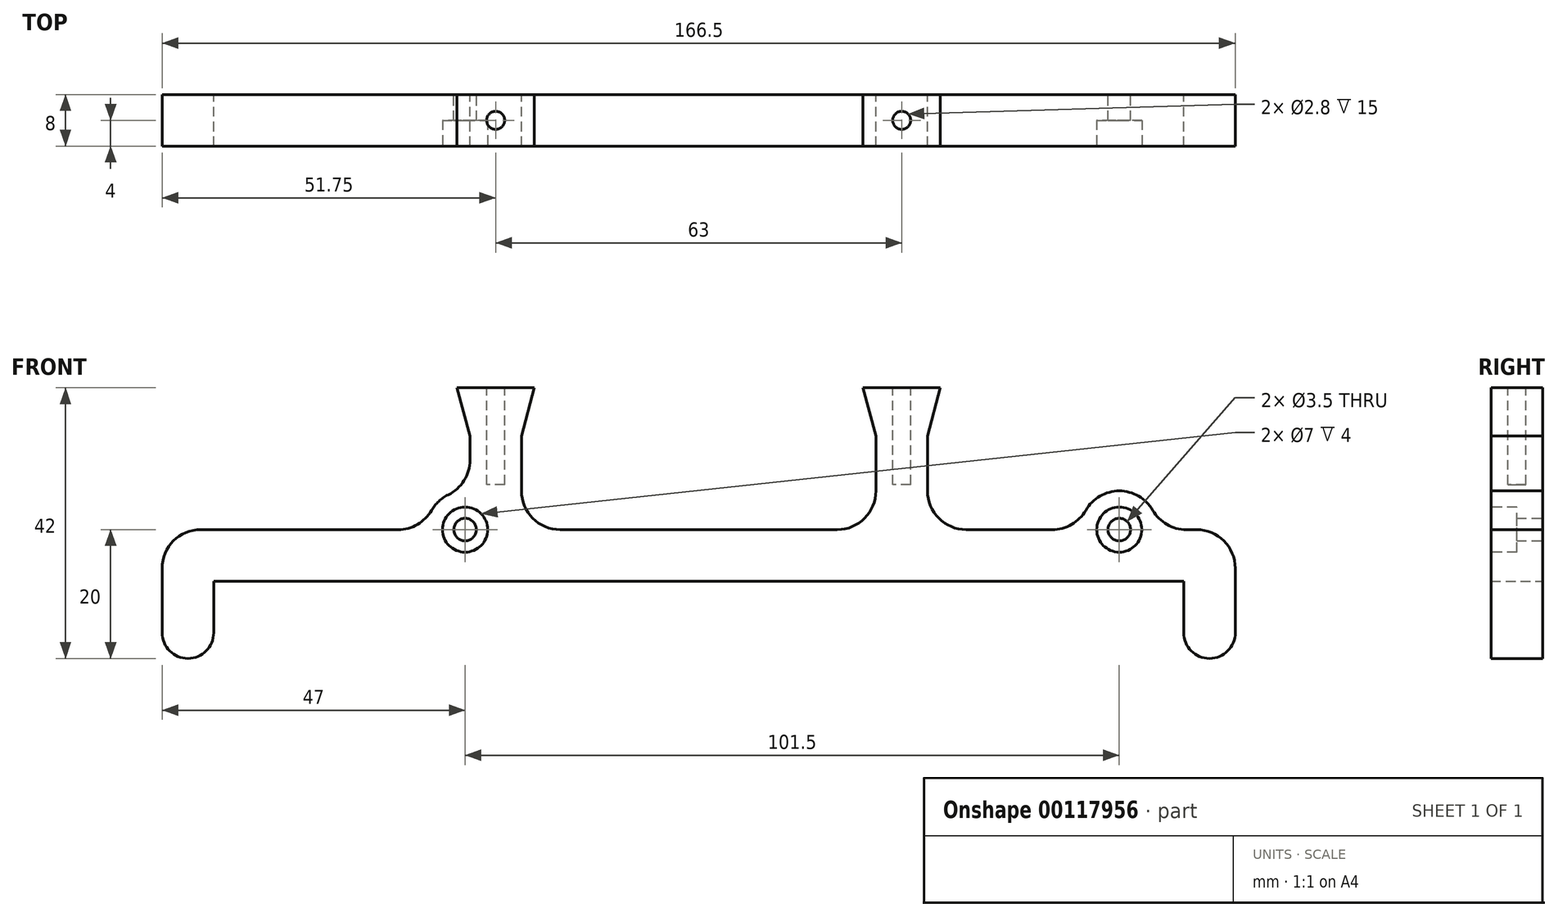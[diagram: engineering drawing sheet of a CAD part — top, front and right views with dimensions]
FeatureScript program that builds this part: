
annotation { "Feature Type Name" : "Feature", "Feature Type Description" : "" }
export const myFeature = defineFeature(function(context is Context, id is Id, definition is map)
    precondition{}
    {
        {
            var Q0;
            Q0=qCreatedBy(makeId("Front.planeOp"),FACE);
            var sketch = newSketch(context, id + "F0", { "sketchPlane" : qUnion([Q0])});
            skLineSegment(sketch, "E0", {"start": v(0, 0) * mm, "end": v(75.25, 0) * mm});
            skLineSegment(sketch, "E1", {"start": v(83.25, -8) * mm, "end": v(83.25, 8) * mm});
            skLineSegment(sketch, "E2", {"start": v(83.25, 8) * mm, "end": v(71.25, 8) * mm});
            skLineSegment(sketch, "E3", {"start": v(0, 58.4) * mm, "end": v(0, -46.84) * mm, "construction": true});
            skLineSegment(sketch, "E4", {"start": v(75.25, 0) * mm, "end": v(75.25, -8) * mm});
            skArc(sketch, "E5", {"start": v(75.25, -8) * mm, "mid": v(79.25, -12) * mm, "end": v(83.25, -8) * mm});
            skLineSegment(sketch, "E6.MirrorCS", {"start": v(-83.25, 8) * mm, "end": v(-42.25, 8) * mm});
            skLineSegment(sketch, "E7.MirrorCS", {"start": v(0, 0) * mm, "end": v(-75.25, 0) * mm});
            skLineSegment(sketch, "E8.MirrorCS", {"start": v(-75.25, 0) * mm, "end": v(-75.25, -8) * mm});
            skLineSegment(sketch, "E9.MirrorCS", {"start": v(-83.25, -8) * mm, "end": v(-83.25, 8) * mm});
            skArc(sketch, "E10.MirrorCS", {"start": v(-75.25, -8) * mm, "mid": v(-79.25, -12) * mm, "end": v(-83.25, -8) * mm});
            skCircle(sketch, "E11", {"center": v(65.25, 8) * mm, "radius": 1.75 * mm});
            skLineSegment(sketch, "E12", {"start": v(59.25, 8) * mm, "end": v(59.25, 8) * mm});
            skLineSegment(sketch, "E13", {"start": v(59.25, 8) * mm, "end": v(35.5, 8) * mm});
            skArc(sketch, "E14", {"start": v(71.25, 8) * mm, "mid": v(65.25, 14) * mm, "end": v(59.25, 8) * mm});
            skCircle(sketch, "E15", {"center": v(-36.25, 8) * mm, "radius": 1.75 * mm});
            skLineSegment(sketch, "E16", {"start": v(35.5, 8) * mm, "end": v(35.5, 30) * mm});
            skLineSegment(sketch, "E17", {"start": v(35.5, 30) * mm, "end": v(27.5, 30) * mm});
            skLineSegment(sketch, "E18", {"start": v(27.5, 30) * mm, "end": v(27.5, 8) * mm});
            skLineSegment(sketch, "E19.MirrorCS", {"start": v(-35.5, 30) * mm, "end": v(-27.5, 30) * mm});
            skLineSegment(sketch, "E20.MirrorCS", {"start": v(-27.5, 30) * mm, "end": v(-27.5, 8) * mm});
            skLineSegment(sketch, "E21", {"start": v(27.5, 8) * mm, "end": v(0, 8) * mm});
            skArc(sketch, "E22", {"start": v(-35.5, 13.95) * mm, "mid": v(-40.22, 12.5) * mm, "end": v(-42.25, 8) * mm});
            skLineSegment(sketch, "E23", {"start": v(-27.5, 8) * mm, "end": v(0, 8) * mm});
            skLineSegment(sketch, "E24", {"start": v(-35.5, 30) * mm, "end": v(-35.5, 13.95) * mm});
            skPoint(sketch, "E25", {"position": v(-31.5, 30) * mm});
            skPoint(sketch, "E26", {"position": v(31.5, 30) * mm});
            skLineSegment(sketch, "E27", {"start": v(27.5, 30) * mm, "end": v(25.5, 30) * mm});
            skLineSegment(sketch, "E28", {"start": v(25.5, 30) * mm, "end": v(27.5, 22.54) * mm});
            skLineSegment(sketch, "E29", {"start": v(31.5, 30) * mm, "end": v(31.5, 23.05) * mm, "construction": true});
            skLineSegment(sketch, "E30.MirrorCS", {"start": v(37.5, 30) * mm, "end": v(35.5, 22.54) * mm});
            skLineSegment(sketch, "E31.MirrorCS", {"start": v(35.5, 30) * mm, "end": v(37.5, 30) * mm});
            skLineSegment(sketch, "E32.MirrorCS", {"start": v(-37.5, 30) * mm, "end": v(-35.5, 22.54) * mm});
            skLineSegment(sketch, "E33.MirrorCS", {"start": v(-35.5, 30) * mm, "end": v(-37.5, 30) * mm});
            skLineSegment(sketch, "E34.MirrorCS", {"start": v(-27.5, 30) * mm, "end": v(-25.5, 30) * mm});
            skLineSegment(sketch, "E35.MirrorCS", {"start": v(-25.5, 30) * mm, "end": v(-27.5, 22.54) * mm});
            skSolve(sketch);
        }
        {
            var Q0;
            Q0=makeQuery(id+"F0.imprint","IMPRINT",FACE,{"disambiguationData":[TD([[makeQuery(id+"F0.imprint","IMPRINT",EDGE,{"derivedFrom":sQuery(id+"F0.wireOp",EDGE,"E0")}),1.0]])]});
            var Q1;
            {var subQ2=sQuery(id+"F0.wireOp",EDGE,"E32.MirrorCS");Q1=makeQuery(id+"F0.imprint","IMPRINT",FACE,{"disambiguationData":[TD([[makeQuery(id+"F0.imprint","IMPRINT",EDGE,{"derivedFrom":subQ2}),1.0]])]});}
            var Q2;
            {var subQ0=sQuery(id+"F0.wireOp",EDGE,"E34.MirrorCS");Q2=makeQuery(id+"F0.imprint","IMPRINT",FACE,{"disambiguationData":[TD([[makeQuery(id+"F0.imprint","IMPRINT",EDGE,{"derivedFrom":subQ0}),-1.0]])]});}
            var Q3;
            {var subQ0=sQuery(id+"F0.wireOp",EDGE,"E27");Q3=makeQuery(id+"F0.imprint","IMPRINT",FACE,{"disambiguationData":[TD([[makeQuery(id+"F0.imprint","IMPRINT",EDGE,{"derivedFrom":subQ0}),1.0]])]});}
            var Q4;
            {var subQ2=sQuery(id+"F0.wireOp",EDGE,"E30.MirrorCS");Q4=makeQuery(id+"F0.imprint","IMPRINT",FACE,{"disambiguationData":[TD([[makeQuery(id+"F0.imprint","IMPRINT",EDGE,{"derivedFrom":subQ2}),-1.0]])]});}
            extrude(context, id + "F1", {"entities" : qUnion([Q0, Q1, Q2, Q3, Q4]), "depth" : 8 * mm});
        }
        {
            var Q0;
            Q0=makeQuery(id+"F1.opExtrude","SWEPT_EDGE",EDGE,{"disambiguationData":[OSD([sQuery(id+"F0.wireOp",EDGE,"E6.MirrorCS"),sQuery(id+"F0.wireOp",EDGE,"489e7f22-d6cf-4f15-957e-4b833c53c52d2")])]});
            var Q1;
            Q1=makeQuery(id+"F1.opExtrude","SWEPT_EDGE",EDGE,{"disambiguationData":[OSD([sQuery(id+"F0.wireOp",EDGE,"489e7f22-d6cf-4f15-957e-4b833c53c52d2"),sQuery(id+"F0.wireOp",EDGE,"Yuy2IKjd-wEt4-qpBP-bmLo-x0tXG2LdxOvr")])]});
            var Q2;
            Q2=makeQuery(id+"F1.opExtrude","SWEPT_EDGE",EDGE,{"disambiguationData":[OSD([sQuery(id+"F0.wireOp",EDGE,"E13"),sQuery(id+"F0.wireOp",EDGE,"E14")])]});
            var Q3;
            Q3=makeQuery(id+"F1.opExtrude","SWEPT_EDGE",EDGE,{"disambiguationData":[OSD([sQuery(id+"F0.wireOp",EDGE,"E2"),sQuery(id+"F0.wireOp",EDGE,"E14")])]});
            var Q4;
            Q4=makeQuery(id+"F1.opExtrude","SWEPT_EDGE",EDGE,{"disambiguationData":[OSD([sQuery(id+"F0.wireOp",EDGE,"E1"),sQuery(id+"F0.wireOp",EDGE,"E2")])]});
            var Q5;
            Q5=makeQuery(id+"F1.opExtrude","SWEPT_EDGE",EDGE,{"disambiguationData":[OSD([sQuery(id+"F0.wireOp",EDGE,"E6.MirrorCS"),sQuery(id+"F0.wireOp",EDGE,"E9.MirrorCS")])]});
            var Q6;
            Q6=makeQuery(id+"F1.opExtrude","SWEPT_EDGE",EDGE,{"disambiguationData":[OSD([sQuery(id+"F0.wireOp",EDGE,"E22"),sQuery(id+"F0.wireOp",EDGE,"E24")])]});
            var Q7;
            Q7=makeQuery(id+"F1.opExtrude","SWEPT_EDGE",EDGE,{"disambiguationData":[OSD([sQuery(id+"F0.wireOp",EDGE,"E20.MirrorCS"),sQuery(id+"F0.wireOp",EDGE,"E23")])]});
            var Q8;
            Q8=makeQuery(id+"F1.opExtrude","SWEPT_EDGE",EDGE,{"disambiguationData":[OSD([sQuery(id+"F0.wireOp",EDGE,"E18"),sQuery(id+"F0.wireOp",EDGE,"E21")])]});
            var Q9;
            Q9=makeQuery(id+"F1.opExtrude","SWEPT_EDGE",EDGE,{"disambiguationData":[OSD([sQuery(id+"F0.wireOp",EDGE,"E13"),sQuery(id+"F0.wireOp",EDGE,"E16")])]});
            fillet(context, id + "F2", {"entities" : qUnion([Q0, Q1, Q2, Q3, Q4, Q5, Q6, Q7, Q8, Q9]), "radius" : 6 * mm, "tangentPropagation" : true, "allowEdgeOverflow" : false});
        }
        {
            var Q0;
            Q0=makeQuery(id+"F1.opExtrude","CAP_FACE",FACE,{"disambiguationData":[OSD([sQuery(id+"F0.wireOp",EDGE,"E0"),sQuery(id+"F0.wireOp",EDGE,"E1"),sQuery(id+"F0.wireOp",EDGE,"E2"),sQuery(id+"F0.wireOp",EDGE,"E4"),sQuery(id+"F0.wireOp",EDGE,"E5"),sQuery(id+"F0.wireOp",EDGE,"E6.MirrorCS"),sQuery(id+"F0.wireOp",EDGE,"E7.MirrorCS"),sQuery(id+"F0.wireOp",EDGE,"E8.MirrorCS"),sQuery(id+"F0.wireOp",EDGE,"E9.MirrorCS"),sQuery(id+"F0.wireOp",EDGE,"E10.MirrorCS"),sQuery(id+"F0.wireOp",EDGE,"E11"),sQuery(id+"F0.wireOp",EDGE,"E13"),sQuery(id+"F0.wireOp",EDGE,"E14"),sQuery(id+"F0.wireOp",EDGE,"E15"),sQuery(id+"F0.wireOp",EDGE,"E16"),sQuery(id+"F0.wireOp",EDGE,"E17"),sQuery(id+"F0.wireOp",EDGE,"E18"),sQuery(id+"F0.wireOp",EDGE,"E19.MirrorCS"),sQuery(id+"F0.wireOp",EDGE,"E20.MirrorCS"),sQuery(id+"F0.wireOp",EDGE,"E21"),sQuery(id+"F0.wireOp",EDGE,"E22"),sQuery(id+"F0.wireOp",EDGE,"E23"),sQuery(id+"F0.wireOp",EDGE,"E24")])],"isStart":false});
            var sketch = newSketch(context, id + "F3", { "sketchPlane" : qUnion([Q0])});
            skCircle(sketch, "E36", {"center": v(-36.25, 8) * mm, "radius": 3.5 * mm});
            skCircle(sketch, "E37", {"center": v(65.25, 8) * mm, "radius": 3.5 * mm});
            skSolve(sketch);
        }
        {
            var Q0;
            Q0 = qSketchRegion(id + "F3", true);
            extrude(context, id + "F4", {"entities" : qUnion([Q0]), "operationType" : NewBodyOperationType.REMOVE, "oppositeDirection" : true, "depth" : 4 * mm});
        }
        {
            var Q0;
            Q0=makeQuery(id+"F1.opExtrude","SWEPT_FACE",FACE,{"disambiguationData":[OSD([sQuery(id+"F0.wireOp",EDGE,"E19.MirrorCS")])]});
            var sketch = newSketch(context, id + "F5", { "sketchPlane" : qUnion([Q0])});
            skCircle(sketch, "E38", {"center": v(-31.5, -4) * mm, "radius": 1.4 * mm});
            skPoint(sketch, "E38.centerSnap0", {"position": v(-35.5, -4) * mm});
            skPoint(sketch, "E38.centerSnap1", {"position": v(-31.5, -8) * mm});
            skSolve(sketch);
        }
        {
            var Q0;
            Q0 = qSketchRegion(id + "F5", true);
            extrude(context, id + "F6", {"entities" : qUnion([Q0]), "operationType" : NewBodyOperationType.REMOVE, "oppositeDirection" : true, "depth" : 15 * mm});
        }
        {
            var Q0;
            Q0=makeQuery(id+"F1.opExtrude","SWEPT_FACE",FACE,{"disambiguationData":[OSD([sQuery(id+"F0.wireOp",EDGE,"E17")])]});
            var sketch = newSketch(context, id + "F7", { "sketchPlane" : qUnion([Q0])});
            skCircle(sketch, "E39", {"center": v(31.5, -4) * mm, "radius": 1.4 * mm});
            skPoint(sketch, "E39.centerSnap0", {"position": v(27.5, -4) * mm});
            skPoint(sketch, "E39.centerSnap1", {"position": v(31.5, -8) * mm});
            skSolve(sketch);
        }
        {
            var Q0;
            Q0 = qSketchRegion(id + "F7", true);
            extrude(context, id + "F8", {"entities" : qUnion([Q0]), "operationType" : NewBodyOperationType.REMOVE, "oppositeDirection" : true, "depth" : 15 * mm});
        }
    });
